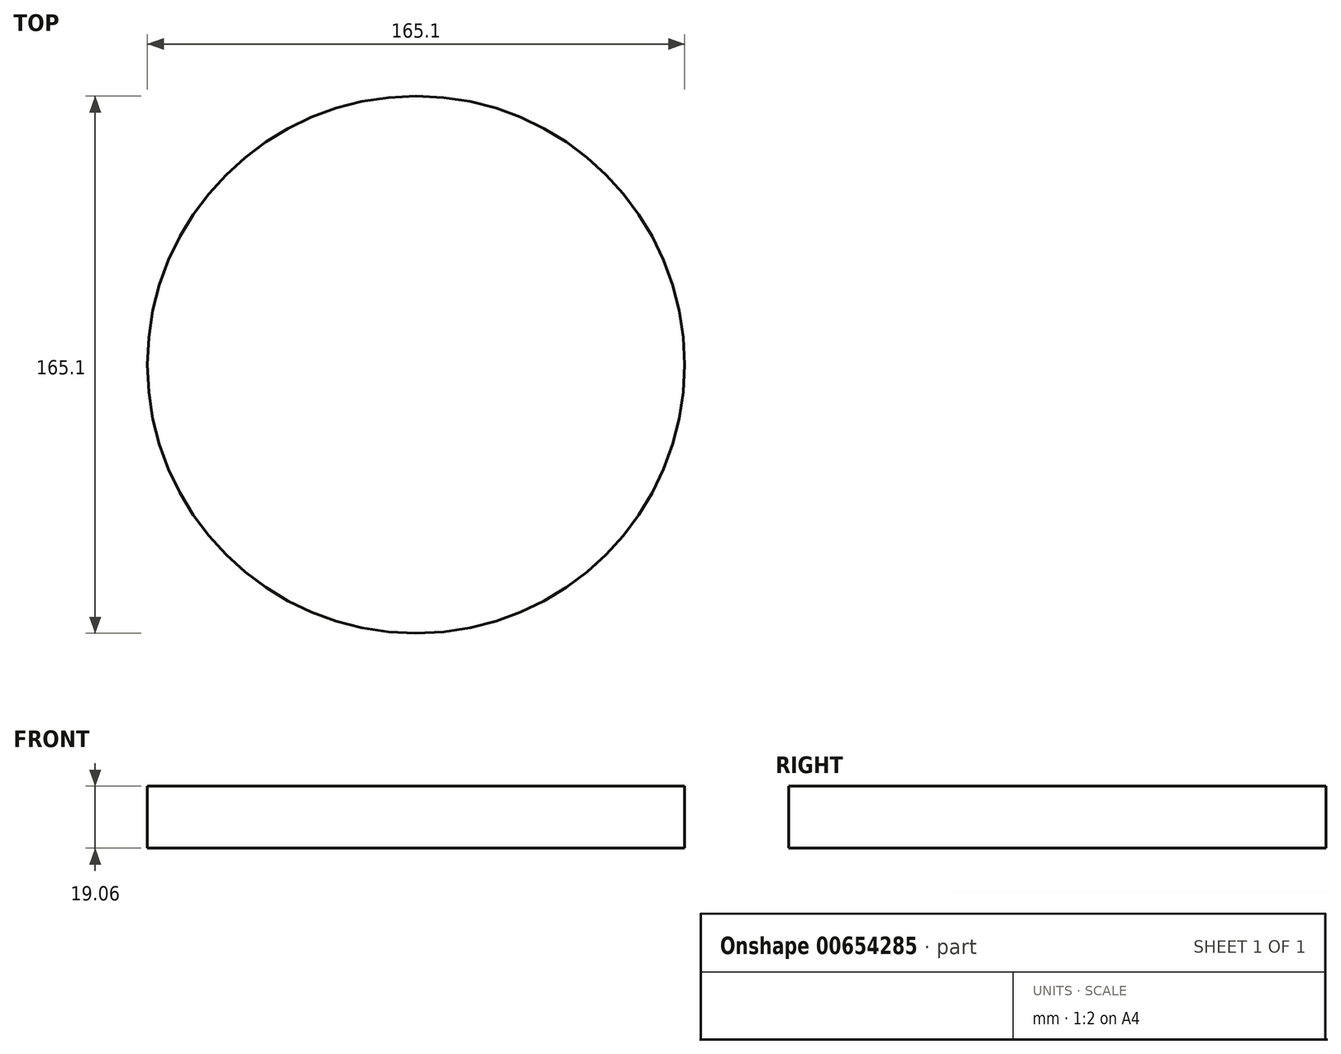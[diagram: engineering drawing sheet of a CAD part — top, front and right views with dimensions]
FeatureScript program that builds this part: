
annotation { "Feature Type Name" : "Feature", "Feature Type Description" : "" }
export const myFeature = defineFeature(function(context is Context, id is Id, definition is map)
    precondition{}
    {
        {
            var Q0;
            Q0=qCreatedBy(makeId("Top.planeOp"),FACE);
            var sketch = newSketch(context, id + "F0", { "sketchPlane" : qUnion([Q0])});
            skCircle(sketch, "E0", {"center": v(0, 0) * mm, "radius": 82.55 * mm});
            skSolve(sketch);
        }
        {
            var Q0;
            Q0 = qSketchRegion(id + "F0", true);
            extrude(context, id + "F1", {"entities" : qUnion([Q0]), "endBound" : BoundingType.SYMMETRIC, "depth" : 19.05 * mm, "offsetDistance" : 25.4 * mm});
        }
    });
